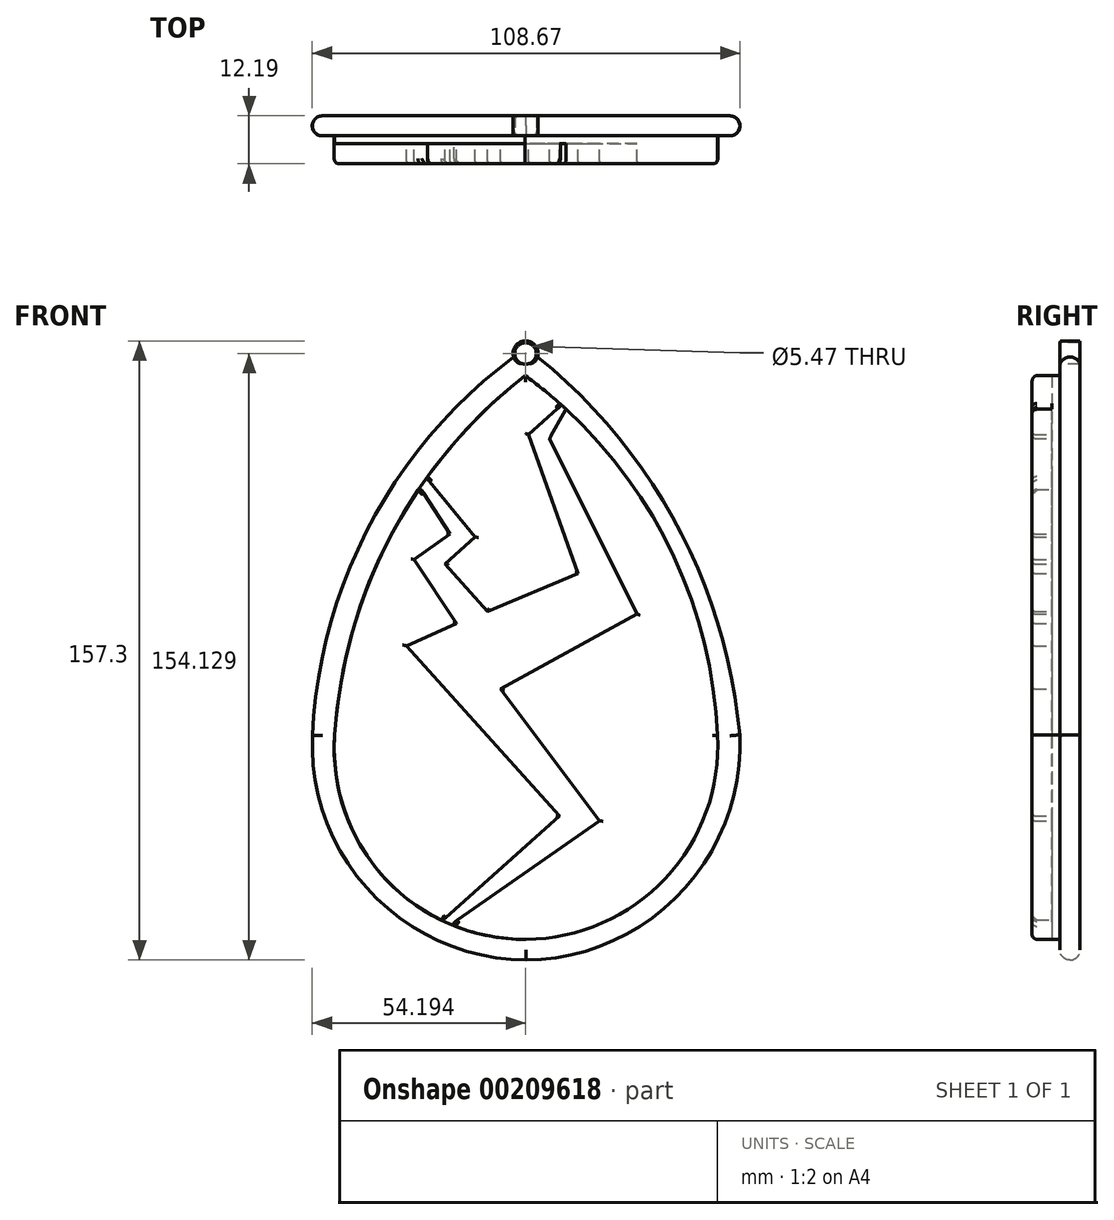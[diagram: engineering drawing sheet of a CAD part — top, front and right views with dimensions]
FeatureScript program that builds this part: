
annotation { "Feature Type Name" : "Feature", "Feature Type Description" : "" }
export const myFeature = defineFeature(function(context is Context, id is Id, definition is map)
    precondition{}
    {
        {
            var Q0;
            Q0=qCreatedBy(makeId("Front.planeOp"),FACE);
            var sketch = newSketch(context, id + "F0", { "sketchPlane" : qUnion([Q0])});
            skArc(sketch, "E0", {"start": v(8.4, 78.12) * mm, "mid": v(-30.17, 35.25) * mm, "end": v(-45.88, -20.24) * mm});
            skArc(sketch, "E1", {"start": v(-45.88, -20.24) * mm, "mid": v(-30.9, -60.37) * mm, "end": v(8.4, -77.4) * mm});
            skArc(sketch, "E2", {"start": v(8.4, -77.4) * mm, "mid": v(47.63, -60.3) * mm, "end": v(62.68, -20.24) * mm});
            skArc(sketch, "E3", {"start": v(62.68, -20.24) * mm, "mid": v(45.88, 34.65) * mm, "end": v(8.4, 78.12) * mm});
            skSolve(sketch);
        }
        {
            var Q0;
            Q0 = qSketchRegion(id + "F0", true);
            extrude(context, id + "F1", {"entities" : qUnion([Q0]), "depth" : 5.08 * mm});
        }
        {
            var Q0;
            Q0=makeQuery(id+"F1.opExtrude","CAP_FACE",FACE,{"disambiguationData":[OSD([sQuery(id+"F0.wireOp",EDGE,"E0"),sQuery(id+"F0.wireOp",EDGE,"E1"),sQuery(id+"F0.wireOp",EDGE,"E2"),sQuery(id+"F0.wireOp",EDGE,"E3")])],"isStart":false});
            var sketch = newSketch(context, id + "F2", { "sketchPlane" : qUnion([Q0])});
            skArc(sketch, "E4", {"start": v(8.17, 71.11) * mm, "mid": v(-25.88, 30.66) * mm, "end": v(-40.23, -20.24) * mm});
            skArc(sketch, "E5", {"start": v(-40.23, -20.24) * mm, "mid": v(-27.3, -56.85) * mm, "end": v(8.4, -72.13) * mm});
            skArc(sketch, "E6", {"start": v(8.4, -72.13) * mm, "mid": v(43.83, -56.6) * mm, "end": v(57.01, -20.24) * mm});
            skArc(sketch, "E7", {"start": v(57.01, -20.24) * mm, "mid": v(42.97, 30.98) * mm, "end": v(8.17, 71.11) * mm});
            skSolve(sketch);
        }
        {
            var Q0;
            Q0 = qSketchRegion(id + "F2", true);
            extrude(context, id + "F3", {"entities" : qUnion([Q0]), "operationType" : NewBodyOperationType.ADD, "depth" : 2.03 * mm});
        }
        {
            var Q0;
            Q0=makeQuery(id+"F3.opExtrude","CAP_FACE",FACE,{"disambiguationData":[OSD([sQuery(id+"F2.wireOp",EDGE,"E4"),sQuery(id+"F2.wireOp",EDGE,"E5"),sQuery(id+"F2.wireOp",EDGE,"E6"),sQuery(id+"F2.wireOp",EDGE,"E7")])],"isStart":false});
            var sketch = newSketch(context, id + "F4", { "sketchPlane" : qUnion([Q0])});
            skLineSegment(sketch, "E8", {"start": v(-18.57, 42.75) * mm, "end": v(-10.95, 30.86) * mm});
            skLineSegment(sketch, "E9", {"start": v(-10.95, 30.86) * mm, "end": v(-20.02, 24.36) * mm});
            skLineSegment(sketch, "E10", {"start": v(-20.02, 24.36) * mm, "end": v(-9.26, 8.1) * mm});
            skLineSegment(sketch, "E11", {"start": v(-9.26, 8.1) * mm, "end": v(-21.94, 2.44) * mm});
            skLineSegment(sketch, "E12", {"start": v(-21.94, 2.44) * mm, "end": v(16.82, -40.71) * mm});
            skLineSegment(sketch, "E13", {"start": v(16.82, -40.71) * mm, "end": v(-12.89, -67.4) * mm});
            skLineSegment(sketch, "E14", {"start": v(-10.69, -68.39) * mm, "end": v(27.04, -42) * mm});
            skLineSegment(sketch, "E15", {"start": v(27.04, -42) * mm, "end": v(1.93, -8.53) * mm});
            skLineSegment(sketch, "E16", {"start": v(1.93, -8.53) * mm, "end": v(36.5, 10.51) * mm});
            skLineSegment(sketch, "E17", {"start": v(36.5, 10.51) * mm, "end": v(14.4, 55.17) * mm});
            skLineSegment(sketch, "E18", {"start": v(14.4, 55.17) * mm, "end": v(18.56, 62.55) * mm});
            skLineSegment(sketch, "E19", {"start": v(-16.93, 45.1) * mm, "end": v(-4.54, 30.06) * mm});
            skLineSegment(sketch, "E20", {"start": v(-4.54, 30.06) * mm, "end": v(-12.16, 23.2) * mm});
            skLineSegment(sketch, "E21", {"start": v(-12.16, 23.2) * mm, "end": v(-1.37, 11.2) * mm});
            skLineSegment(sketch, "E22", {"start": v(-1.37, 11.2) * mm, "end": v(21.55, 20.76) * mm});
            skLineSegment(sketch, "E23", {"start": v(21.55, 20.76) * mm, "end": v(9.02, 56.14) * mm});
            skLineSegment(sketch, "E24", {"start": v(9.02, 56.14) * mm, "end": v(17.44, 63.58) * mm});
            skArc(sketch, "E25", {"start": v(8.17, 71.11) * mm, "mid": v(-25.8, 30.6) * mm, "end": v(-40.23, -20.24) * mm});
            skArc(sketch, "E26", {"start": v(57.01, -20.24) * mm, "mid": v(42.98, 30.99) * mm, "end": v(8.17, 71.11) * mm});
            skArc(sketch, "E27", {"start": v(8.4, -72.13) * mm, "mid": v(43.83, -56.61) * mm, "end": v(57.01, -20.24) * mm});
            skArc(sketch, "E28", {"start": v(-40.23, -20.24) * mm, "mid": v(-27.26, -56.82) * mm, "end": v(8.4, -72.13) * mm});
            skSolve(sketch);
        }
        {
            var Q0;
            {var subQ0=sQuery(id+"F4.wireOp",EDGE,"E9");Q0=makeQuery(id+"F4.imprint","IMPRINT",FACE,{"disambiguationData":[TD([[makeQuery(id+"F4.imprint","IMPRINT",EDGE,{"derivedFrom":subQ0}),-1.0]])]});}
            var Q1;
            {var subQ1=sQuery(id+"F4.wireOp",EDGE,"E20");Q1=makeQuery(id+"F4.imprint","IMPRINT",FACE,{"disambiguationData":[TD([[makeQuery(id+"F4.imprint","IMPRINT",EDGE,{"derivedFrom":subQ1}),1.0]])]});}
            var Q2;
            {var subQ0=sQuery(id+"F4.wireOp",EDGE,"E15");Q2=makeQuery(id+"F4.imprint","IMPRINT",FACE,{"disambiguationData":[TD([[makeQuery(id+"F4.imprint","IMPRINT",EDGE,{"derivedFrom":subQ0}),-1.0]])]});}
            extrude(context, id + "F5", {"entities" : qUnion([Q0, Q1, Q2]), "operationType" : NewBodyOperationType.ADD, "depth" : 5.08 * mm});
        }
        {
            var Q0;
            Q0=makeQuery(id+"F1.opExtrude","CAP_EDGE",EDGE,{"disambiguationData":[OSD([sQuery(id+"F0.wireOp",EDGE,"E0")])],"isStart":true});
            var Q1;
            Q1=makeQuery(id+"F1.opExtrude","CAP_EDGE",EDGE,{"disambiguationData":[OSD([sQuery(id+"F0.wireOp",EDGE,"E0")])],"isStart":false});
            var Q2;
            Q2=makeQuery(id+"F1.opExtrude","CAP_EDGE",EDGE,{"disambiguationData":[OSD([sQuery(id+"F0.wireOp",EDGE,"E3")])],"isStart":false});
            var Q3;
            Q3=makeQuery(id+"F1.opExtrude","CAP_EDGE",EDGE,{"disambiguationData":[OSD([sQuery(id+"F0.wireOp",EDGE,"E3")])],"isStart":true});
            var Q4;
            Q4=makeQuery(id+"F1.opExtrude","SWEPT_EDGE",EDGE,{"disambiguationData":[OSD([sQuery(id+"F0.wireOp",EDGE,"E0"),sQuery(id+"F0.wireOp",EDGE,"E3")])]});
            fillet(context, id + "F6", {"entities" : qUnion([Q0, Q1, Q2, Q3, Q4]), "radius" : 2.54 * mm, "tangentPropagation" : true, "allowEdgeOverflow" : false});
        }
        {
            var Q0;
            {var subQ0=sQuery(id+"F4.wireOp",EDGE,"E25");Q0=makeQuery(id+"F5.opExtrude","CAP_EDGE",EDGE,{"disambiguationData":[OSD([subQ0]),TDD([makeQuery(id+"F4.imprint","IMPRINT",EDGE,{"disambiguationData":[TD([[makeQuery(id+"F4.imprint","INTERSECT",VERTEX,{"derivedFrom":[sQuery(id+"F4.wireOp",EDGE,"E8"),subQ0]}),-1.0]])],"derivedFrom":subQ0})])],"isStart":false});}
            var Q1;
            {var subQ0=sQuery(id+"F4.wireOp",EDGE,"E28");Q1=makeQuery(id+"F5.opExtrude","CAP_EDGE",EDGE,{"disambiguationData":[OSD([subQ0]),TDD([makeQuery(id+"F4.imprint","IMPRINT",EDGE,{"disambiguationData":[TD([[makeQuery(id+"F4.imprint","INTERSECT",VERTEX,{"derivedFrom":[sQuery(id+"F4.wireOp",EDGE,"E13"),subQ0]}),1.0]])],"derivedFrom":subQ0})])],"isStart":false});}
            var Q2;
            Q2=makeQuery(id+"F5.opExtrude","CAP_EDGE",EDGE,{"disambiguationData":[OSD([sQuery(id+"F2.wireOp",EDGE,"E6")])],"isStart":false});
            var Q3;
            {var subQ0=sQuery(id+"F4.wireOp",EDGE,"E28");Q3=makeQuery(id+"F5.opExtrude","CAP_EDGE",EDGE,{"disambiguationData":[OSD([subQ0]),TDD([makeQuery(id+"F4.imprint","IMPRINT",EDGE,{"disambiguationData":[TD([[makeQuery(id+"F4.imprint","INTERSECT",VERTEX,{"derivedFrom":[sQuery(id+"F4.wireOp",EDGE,"E14"),subQ0]}),-1.0]])],"derivedFrom":subQ0})])],"isStart":false});}
            var Q4;
            {var subQ0=sQuery(id+"F2.wireOp",EDGE,"E7");var subQ1=makeQuery(id+"F3.opExtrude","CAP_EDGE",EDGE,{"disambiguationData":[OSD([subQ0])],"isStart":false});Q4=makeQuery(id+"F5.opExtrude","CAP_EDGE",EDGE,{"disambiguationData":[OSD([subQ0]),TDD([makeQuery(id+"F4.imprint","IMPRINT",EDGE,{"disambiguationData":[TD([[makeQuery(id+"F4.imprint","INTERSECT",VERTEX,{"derivedFrom":[subQ1,sQuery(id+"F4.wireOp",EDGE,"E18")]}),1.0]])],"derivedFrom":subQ1})])],"isStart":false});}
            var Q5;
            {var subQ0=sQuery(id+"F2.wireOp",EDGE,"E7");var subQ1=makeQuery(id+"F3.opExtrude","CAP_EDGE",EDGE,{"disambiguationData":[OSD([subQ0])],"isStart":false});Q5=makeQuery(id+"F5.opExtrude","CAP_EDGE",EDGE,{"disambiguationData":[OSD([subQ0]),TDD([makeQuery(id+"F4.imprint","IMPRINT",EDGE,{"disambiguationData":[TD([[makeQuery(id+"F4.imprint","INTERSECT",VERTEX,{"derivedFrom":[subQ1,sQuery(id+"F4.wireOp",EDGE,"E24")]}),-1.0]])],"derivedFrom":subQ1})])],"isStart":false});}
            var Q6;
            {var subQ0=sQuery(id+"F4.wireOp",EDGE,"E25");Q6=makeQuery(id+"F5.opExtrude","CAP_EDGE",EDGE,{"disambiguationData":[OSD([subQ0]),TDD([makeQuery(id+"F4.imprint","IMPRINT",EDGE,{"disambiguationData":[TD([[makeQuery(id+"F4.imprint","INTERSECT",VERTEX,{"derivedFrom":[sQuery(id+"F4.wireOp",EDGE,"E19"),subQ0]}),1.0]])],"derivedFrom":subQ0})])],"isStart":false});}
            fillet(context, id + "F7", {"entities" : qUnion([Q0, Q1, Q2, Q3, Q4, Q5, Q6]), "radius" : 1.27 * mm, "tangentPropagation" : true, "allowEdgeOverflow" : false});
        }
        {
            var Q0;
            Q0=makeQuery(id+"F5.opExtrude","CAP_EDGE",EDGE,{"disambiguationData":[OSD([sQuery(id+"F4.wireOp",EDGE,"E17")])],"isStart":false});
            var Q1;
            Q1=makeQuery(id+"F5.opExtrude","CAP_EDGE",EDGE,{"disambiguationData":[OSD([sQuery(id+"F4.wireOp",EDGE,"E23")])],"isStart":false});
            var Q2;
            Q2=makeQuery(id+"F5.opExtrude","CAP_EDGE",EDGE,{"disambiguationData":[OSD([sQuery(id+"F4.wireOp",EDGE,"E24")])],"isStart":false});
            var Q3;
            Q3=makeQuery(id+"F5.opExtrude","CAP_EDGE",EDGE,{"disambiguationData":[OSD([sQuery(id+"F4.wireOp",EDGE,"E16")])],"isStart":false});
            var Q4;
            Q4=makeQuery(id+"F5.opExtrude","CAP_EDGE",EDGE,{"disambiguationData":[OSD([sQuery(id+"F4.wireOp",EDGE,"E22")])],"isStart":false});
            var Q5;
            Q5=makeQuery(id+"F5.opExtrude","CAP_EDGE",EDGE,{"disambiguationData":[OSD([sQuery(id+"F4.wireOp",EDGE,"E21")])],"isStart":false});
            var Q6;
            Q6=makeQuery(id+"F5.opExtrude","CAP_EDGE",EDGE,{"disambiguationData":[OSD([sQuery(id+"F4.wireOp",EDGE,"E20")])],"isStart":false});
            var Q7;
            Q7=makeQuery(id+"F5.opExtrude","CAP_EDGE",EDGE,{"disambiguationData":[OSD([sQuery(id+"F4.wireOp",EDGE,"E19")])],"isStart":false});
            var Q8;
            Q8=makeQuery(id+"F5.opExtrude","CAP_EDGE",EDGE,{"disambiguationData":[OSD([sQuery(id+"F4.wireOp",EDGE,"E8")])],"isStart":false});
            var Q9;
            Q9=makeQuery(id+"F5.opExtrude","CAP_EDGE",EDGE,{"disambiguationData":[OSD([sQuery(id+"F4.wireOp",EDGE,"E9")])],"isStart":false});
            var Q10;
            Q10=makeQuery(id+"F5.opExtrude","CAP_EDGE",EDGE,{"disambiguationData":[OSD([sQuery(id+"F4.wireOp",EDGE,"E10")])],"isStart":false});
            var Q11;
            Q11=makeQuery(id+"F5.opExtrude","CAP_EDGE",EDGE,{"disambiguationData":[OSD([sQuery(id+"F4.wireOp",EDGE,"E11")])],"isStart":false});
            var Q12;
            Q12=makeQuery(id+"F5.opExtrude","CAP_EDGE",EDGE,{"disambiguationData":[OSD([sQuery(id+"F4.wireOp",EDGE,"E12")])],"isStart":false});
            var Q13;
            Q13=makeQuery(id+"F5.opExtrude","CAP_EDGE",EDGE,{"disambiguationData":[OSD([sQuery(id+"F4.wireOp",EDGE,"E13")])],"isStart":false});
            var Q14;
            Q14=makeQuery(id+"F5.opExtrude","CAP_EDGE",EDGE,{"disambiguationData":[OSD([sQuery(id+"F4.wireOp",EDGE,"E14")])],"isStart":false});
            var Q15;
            Q15=makeQuery(id+"F5.opExtrude","CAP_EDGE",EDGE,{"disambiguationData":[OSD([sQuery(id+"F4.wireOp",EDGE,"E15")])],"isStart":false});
            fillet(context, id + "F8", {"entities" : qUnion([Q0, Q1, Q2, Q3, Q4, Q5, Q6, Q7, Q8, Q9, Q10, Q11, Q12, Q13, Q14, Q15]), "radius" : 0.64 * mm, "tangentPropagation" : true, "allowEdgeOverflow" : false});
        }
        {
            var Q0;
            Q0=makeQuery(id+"F1.opExtrude","CAP_EDGE",EDGE,{"disambiguationData":[OSD([sQuery(id+"F0.wireOp",EDGE,"E1")])],"isStart":false});
            var Q1;
            Q1=makeQuery(id+"F1.opExtrude","CAP_EDGE",EDGE,{"disambiguationData":[OSD([sQuery(id+"F0.wireOp",EDGE,"E2")])],"isStart":false});
            fillet(context, id + "F9", {"entities" : qUnion([Q0, Q1]), "radius" : 2.54 * mm, "tangentPropagation" : true, "allowEdgeOverflow" : false});
        }
        {
            var Q0;
            Q0=makeQuery(id+"F1.opExtrude","CAP_FACE",FACE,{"disambiguationData":[OSD([sQuery(id+"F0.wireOp",EDGE,"E0"),sQuery(id+"F0.wireOp",EDGE,"E1"),sQuery(id+"F0.wireOp",EDGE,"E2"),sQuery(id+"F0.wireOp",EDGE,"E3")])],"isStart":false});
            var sketch = newSketch(context, id + "F10", { "sketchPlane" : qUnion([Q0])});
            skCircle(sketch, "E29", {"center": v(8.25, 76.73) * mm, "radius": 3.18 * mm});
            skSolve(sketch);
        }
        {
            var Q0;
            {var subQ0=sQuery(id+"F10.wireOp",EDGE,"E29");var subQ1=sQuery(id+"F0.wireOp",EDGE,"E3");var subQ2=sQuery(id+"F0.wireOp",EDGE,"E0");var subQ3=makeQuery(id+"F1.opExtrude","CAP_FACE",FACE,{"disambiguationData":[OSD([subQ2,sQuery(id+"F0.wireOp",EDGE,"E1"),sQuery(id+"F0.wireOp",EDGE,"E2"),subQ1])],"isStart":false});var subQ4=makeQuery(id+"F6.opFillet","BLEND_EDGE",EDGE,{"blendedFrom":[makeQuery(id+"F1.opExtrude","CAP_EDGE",EDGE,{"disambiguationData":[OSD([subQ1])],"isStart":false}),subQ3],"blendedInto":[subQ3]});var subQ5=makeQuery(id+"F10.imprint","INTERSECT",VERTEX,{"derivedFrom":[subQ4,subQ0]});Q0=makeQuery(id+"F10.imprint","IMPRINT",FACE,{"disambiguationData":[TD([[makeQuery(id+"F10.imprint","IMPRINT",EDGE,{"disambiguationData":[TD([[subQ5,-1.0]])],"derivedFrom":subQ0}),1.0]])]});}
            var Q1;
            {var subQ0=sQuery(id+"F0.wireOp",EDGE,"E3");var subQ1=sQuery(id+"F0.wireOp",EDGE,"E0");Q1=makeQuery(id+"F6.opFillet","BLEND_VERTEX",VERTEX,{"blendedFrom":[makeQuery(id+"F1.opExtrude","CAP_VERTEX",VERTEX,{"disambiguationData":[OSD([subQ1,subQ0])],"isStart":true}),makeQuery(id+"F1.opExtrude","CAP_EDGE",EDGE,{"disambiguationData":[OSD([subQ1])],"isStart":true}),makeQuery(id+"F1.opExtrude","CAP_EDGE",EDGE,{"disambiguationData":[OSD([subQ0])],"isStart":true}),makeQuery(id+"F1.opExtrude","CAP_FACE",FACE,{"disambiguationData":[OSD([subQ1,sQuery(id+"F0.wireOp",EDGE,"E1"),sQuery(id+"F0.wireOp",EDGE,"E2"),subQ0])],"isStart":true})],"blendedInto":[makeQuery(id+"F1.opExtrude","CAP_FACE",FACE,{"disambiguationData":[OSD([subQ1,sQuery(id+"F0.wireOp",EDGE,"E1"),sQuery(id+"F0.wireOp",EDGE,"E2"),subQ0])],"isStart":true})]});}
            extrude(context, id + "F11", {"entities" : qUnion([Q0]), "operationType" : NewBodyOperationType.ADD, "endBound" : BoundingType.UP_TO_VERTEX, "oppositeDirection" : true, "endBoundEntityVertex" : qUnion([Q1]), "depth" : 25.4 * mm});
        }
        {
            var Q0;
            Q0=makeQuery(id+"F11.opExtrude","CAP_EDGE",EDGE,{"disambiguationData":[OSD([sQuery(id+"F10.wireOp",EDGE,"E29")])],"isStart":true});
            var Q1;
            {var subQ0=sQuery(id+"F10.wireOp",EDGE,"E29");var subQ1=sQuery(id+"F0.wireOp",EDGE,"E3");var subQ2=sQuery(id+"F0.wireOp",EDGE,"E0");var subQ3=makeQuery(id+"F1.opExtrude","CAP_FACE",FACE,{"disambiguationData":[OSD([subQ2,sQuery(id+"F0.wireOp",EDGE,"E1"),sQuery(id+"F0.wireOp",EDGE,"E2"),subQ1])],"isStart":false});Q1=makeQuery(id+"F11.opExtrude","TWEAK_EDGE",EDGE,{"derivedFrom":[makeQuery(id+"F10.imprint","IMPRINT",EDGE,{"disambiguationData":[TD([[makeQuery(id+"F10.imprint","INTERSECT",VERTEX,{"derivedFrom":[makeQuery(id+"F6.opFillet","BLEND_EDGE",EDGE,{"blendedFrom":[makeQuery(id+"F1.opExtrude","CAP_EDGE",EDGE,{"disambiguationData":[OSD([subQ1])],"isStart":false}),subQ3],"blendedInto":[subQ3]}),subQ0]}),-1.0]])],"derivedFrom":subQ0}),dummyQuery(id+"F11.vertexPlane.planeOp",FACE)]});}
            fillet(context, id + "F12", {"entities" : qUnion([Q0, Q1]), "radius" : 0.38 * mm, "tangentPropagation" : true, "allowEdgeOverflow" : false});
        }
        {
            var Q0;
            {var subQ0=sQuery(id+"F0.wireOp",EDGE,"E3");var subQ1=sQuery(id+"F0.wireOp",EDGE,"E2");var subQ2=sQuery(id+"F0.wireOp",EDGE,"E1");var subQ3=sQuery(id+"F0.wireOp",EDGE,"E0");Q0=makeQuery(id+"F11.boolean.opBoolean","MERGE",FACE,{"derivedFrom":[makeQuery(id+"F1.opExtrude","CAP_FACE",FACE,{"disambiguationData":[OSD([subQ3,subQ2,subQ1,subQ0])],"isStart":false}),makeQuery(id+"F11.opExtrude","CAP_FACE",FACE,{"disambiguationData":[OSD([subQ3,subQ2,subQ1,subQ0,sQuery(id+"F10.wireOp",EDGE,"E29")])],"isStart":true})]});}
            var sketch = newSketch(context, id + "F13", { "sketchPlane" : qUnion([Q0])});
            skCircle(sketch, "E30", {"center": v(8.25, 76.73) * mm, "radius": 2.74 * mm});
            skSolve(sketch);
        }
        {
            var Q0;
            Q0=makeQuery(id+"F13.imprint","IMPRINT",FACE,{"disambiguationData":[TD([[makeQuery(id+"F13.imprint","IMPRINT",EDGE,{"derivedFrom":sQuery(id+"F13.wireOp",EDGE,"E30")}),1.0]])]});
            extrude(context, id + "F14", {"entities" : qUnion([Q0]), "operationType" : NewBodyOperationType.REMOVE, "endBound" : BoundingType.THROUGH_ALL, "oppositeDirection" : true, "depth" : 25.4 * mm});
        }
        {
            var Q0;
            Q0=makeQuery(id+"F14.boolean.opBoolean","INTERSECT",EDGE,{"derivedFrom":[makeQuery(id+"F11.boolean.opBoolean","MERGE",FACE,{"derivedFrom":[makeQuery(id+"F1.opExtrude","CAP_FACE",FACE,{"disambiguationData":[OSD([sQuery(id+"F0.wireOp",EDGE,"E0"),sQuery(id+"F0.wireOp",EDGE,"E1"),sQuery(id+"F0.wireOp",EDGE,"E2"),sQuery(id+"F0.wireOp",EDGE,"E3")])],"isStart":true}),makeQuery(id+"F11.opExtrude","CAP_FACE",FACE,{"disambiguationData":[OSD([dummyQuery(id+"F11.vertexPlane.planeOp",FACE)])],"isStart":false})]}),makeQuery(id+"F14.opExtrude","SWEPT_FACE",FACE,{"disambiguationData":[OSD([sQuery(id+"F13.wireOp",EDGE,"E30")])]})]});
            var Q1;
            Q1=makeQuery(id+"F14.boolean.opBoolean","COPY",EDGE,{"derivedFrom":makeQuery(id+"F14.opExtrude","CAP_EDGE",EDGE,{"disambiguationData":[OSD([sQuery(id+"F13.wireOp",EDGE,"E30")])],"isStart":true})});
            fillet(context, id + "F15", {"entities" : qUnion([Q0, Q1]), "radius" : 0.04 * mm, "tangentPropagation" : true, "allowEdgeOverflow" : false});
        }
    });
